# Revit family: QF_Vollrath 72165
name_source: partatom
category: Specialty Equipment
revit_build: Autodesk Revit 2016 (Build: 20151007_0715(x64)
units: mm (PartAtom-declared; Revit-internal decimal feet)

## family parameters
Always vertical = Yes
Cut with Voids When Loaded = No
OmniClass Number = 23.40.40.11.21
OmniClass Title = Hot Cabinets
Part Type = Normal
Room Calculation Point = No
Round Connector Dimension = Use Diameter
Shared = No
Work Plane-Based = No

## types (2) — shared parameters
Apparent Power = 648 VA
Assembly Code = E1090320
CSI MasterFormat = 11 42 13
Conn Plug = NEMA 5-15P
Cycle = 60 Hz
Description = Colonial Kettle
Elec Conn Connection Height = 2 "
FL Amps = 5 A
Manufacturer = Vollrath
Phase = 1
URL = www.vollrathco.com
Volts = 120 V
Watts = 650 W
Weight in Pounds = 23.4
Width = 15.8 "

## per-type parameters (varying)
| type | Kettle Finish |
| 72166 | QF_Finishes_Burnt Copper |
| 72165 | QF_Finishes_Black |

note: column(s) folded — value = type name in every type: Model

## geometry (parser evidence)
native form markers: Blend x9, Sweep x2
no freeform markers — native parametric forms only
